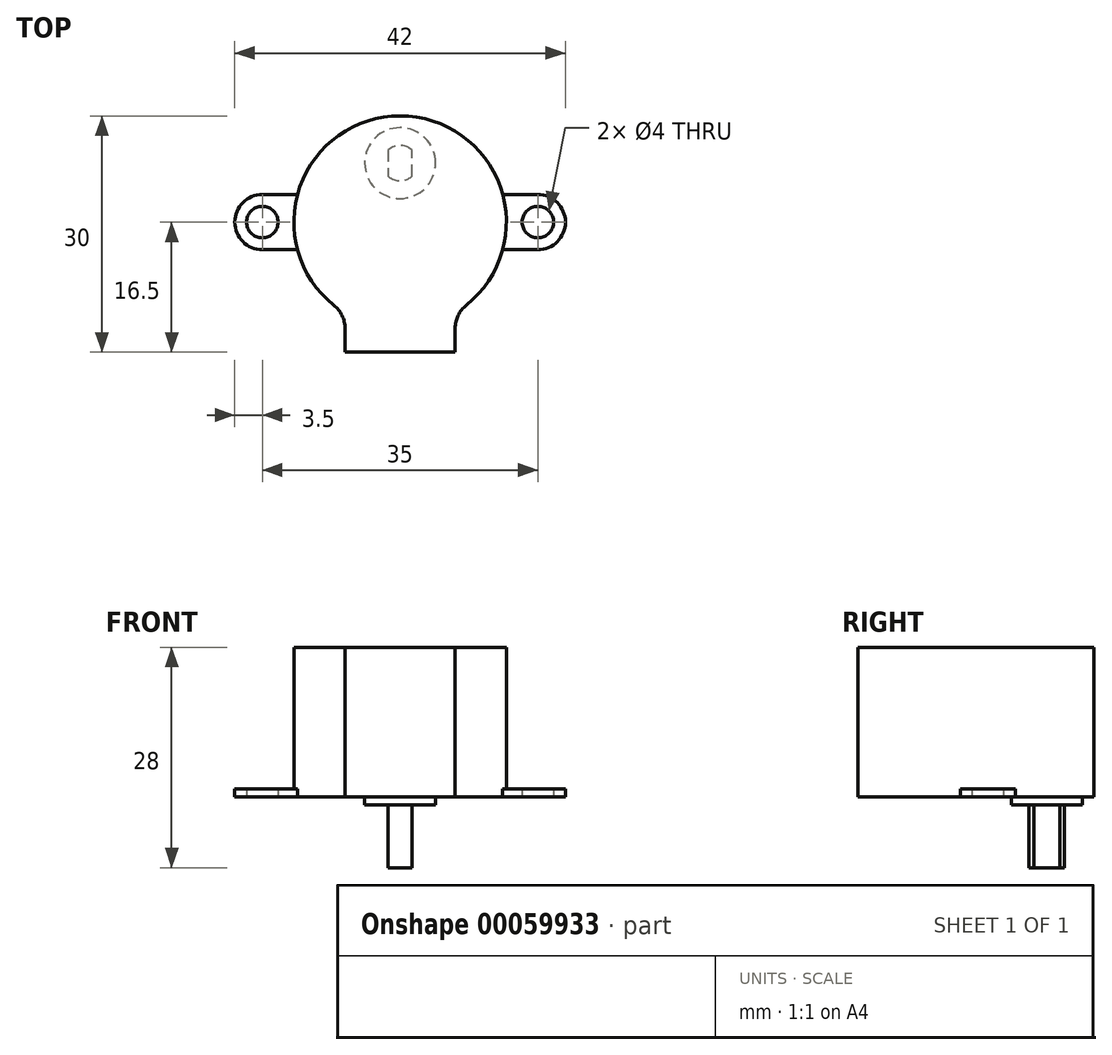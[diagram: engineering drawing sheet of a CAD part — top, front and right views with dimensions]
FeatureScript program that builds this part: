
annotation { "Feature Type Name" : "Feature", "Feature Type Description" : "" }
export const myFeature = defineFeature(function(context is Context, id is Id, definition is map)
    precondition{}
    {
        {
            var Q0;
            Q0=qCreatedBy(makeId("Top.planeOp"),FACE);
            var sketch = newSketch(context, id + "F0", { "sketchPlane" : qUnion([Q0])});
            skArc(sketch, "E0", {"start": v(8.42, -10.55) * mm, "mid": v(0, 13.5) * mm, "end": v(-8.42, -10.55) * mm});
            skLineSegment(sketch, "E1.bottom", {"start": v(-7, -13.5) * mm, "end": v(7, -13.5) * mm, "construction": true});
            skLineSegment(sketch, "E1.top", {"start": v(-7, -16.5) * mm, "end": v(7, -16.5) * mm});
            skLineSegment(sketch, "E1.left", {"start": v(-7, -13.5) * mm, "end": v(-7, -16.5) * mm});
            skLineSegment(sketch, "E1.right", {"start": v(7, -13.5) * mm, "end": v(7, -16.5) * mm});
            skLineSegment(sketch, "E2", {"start": v(0, -13.5) * mm, "end": v(0, -16.5) * mm, "construction": true});
            skArc(sketch, "E3", {"start": v(-7, -13.5) * mm, "mid": v(-7.37, -11.86) * mm, "end": v(-8.42, -10.55) * mm});
            skArc(sketch, "E4.MirrorCS", {"start": v(7, -13.5) * mm, "mid": v(7.37, -11.86) * mm, "end": v(8.42, -10.55) * mm});
            skSolve(sketch);
        }
        {
            var Q0;
            Q0=makeQuery(id+"F0.imprint","IMPRINT",FACE,{"disambiguationData":[TD([[makeQuery(id+"F0.imprint","IMPRINT",EDGE,{"derivedFrom":sQuery(id+"F0.wireOp",EDGE,"E0")}),1.0]])]});
            extrude(context, id + "F1", {"entities" : qUnion([Q0]), "depth" : 19 * mm});
        }
        {
            var Q0;
            Q0=qCreatedBy(makeId("Top.planeOp"),FACE);
            var sketch = newSketch(context, id + "F2", { "sketchPlane" : qUnion([Q0])});
            skCircle(sketch, "E5", {"center": v(17.5, 0) * mm, "radius": 2 * mm});
            skLineSegment(sketch, "E6", {"start": v(13.04, -3.5) * mm, "end": v(17.5, -3.5) * mm});
            skLineSegment(sketch, "E7", {"start": v(13.04, 3.5) * mm, "end": v(17.5, 3.5) * mm});
            skArc(sketch, "E8", {"start": v(17.5, -3.5) * mm, "mid": v(21, 0) * mm, "end": v(17.5, 3.5) * mm});
            skLineSegment(sketch, "E9", {"start": v(17.5, -3.5) * mm, "end": v(17.5, 0) * mm, "construction": true});
            skArc(sketch, "E10", {"start": v(13.04, -3.5) * mm, "mid": v(13.5, 0) * mm, "end": v(13.04, 3.5) * mm});
            skLineSegment(sketch, "E11.MirrorCS", {"start": v(-13.04, -3.5) * mm, "end": v(-17.5, -3.5) * mm});
            skArc(sketch, "E12.MirrorCS", {"start": v(-17.5, -3.5) * mm, "mid": v(-21, 0) * mm, "end": v(-17.5, 3.5) * mm});
            skCircle(sketch, "E13.MirrorC", {"center": v(-17.5, 0) * mm, "radius": 2 * mm});
            skLineSegment(sketch, "E14.MirrorCS", {"start": v(-13.04, 3.5) * mm, "end": v(-17.5, 3.5) * mm});
            skArc(sketch, "E15.MirrorCS", {"start": v(-13.04, -3.5) * mm, "mid": v(-13.5, 0) * mm, "end": v(-13.04, 3.5) * mm});
            skSolve(sketch);
        }
        {
            var Q0;
            Q0 = qSketchRegion(id + "F2", true);
            extrude(context, id + "F3", {"entities" : qUnion([Q0]), "operationType" : NewBodyOperationType.ADD, "depth" : 1 * mm});
        }
        {
            var Q0;
            Q0=makeQuery(id+"F3.boolean.opBoolean","MERGE",FACE,{"derivedFrom":[makeQuery(id+"F1.opExtrude","CAP_FACE",FACE,{"disambiguationData":[OSD([sQuery(id+"F0.wireOp",EDGE,"E0"),sQuery(id+"F0.wireOp",EDGE,"E1.top"),sQuery(id+"F0.wireOp",EDGE,"E1.left"),sQuery(id+"F0.wireOp",EDGE,"E1.right"),sQuery(id+"F0.wireOp",EDGE,"E3"),sQuery(id+"F0.wireOp",EDGE,"E4.MirrorCS")])],"isStart":true}),makeQuery(id+"F3.opExtrude","CAP_FACE",FACE,{"disambiguationData":[OSD([sQuery(id+"F2.wireOp",EDGE,"E5"),sQuery(id+"F2.wireOp",EDGE,"E6"),sQuery(id+"F2.wireOp",EDGE,"E7"),sQuery(id+"F2.wireOp",EDGE,"E8"),sQuery(id+"F2.wireOp",EDGE,"E10")])],"isStart":true}),makeQuery(id+"F3.opExtrude","CAP_FACE",FACE,{"disambiguationData":[OSD([sQuery(id+"F2.wireOp",EDGE,"E11.MirrorCS"),sQuery(id+"F2.wireOp",EDGE,"E12.MirrorCS"),sQuery(id+"F2.wireOp",EDGE,"E13.MirrorC"),sQuery(id+"F2.wireOp",EDGE,"E14.MirrorCS"),sQuery(id+"F2.wireOp",EDGE,"E15.MirrorCS")])],"isStart":true})]});
            var sketch = newSketch(context, id + "F4", { "sketchPlane" : qUnion([Q0])});
            skCircle(sketch, "E16", {"center": v(0, -7.5) * mm, "radius": 4.5 * mm});
            skSolve(sketch);
        }
        {
            var Q0;
            Q0=makeQuery(id+"F4.imprint","IMPRINT",FACE,{"disambiguationData":[TD([[makeQuery(id+"F4.imprint","IMPRINT",EDGE,{"derivedFrom":sQuery(id+"F4.wireOp",EDGE,"E16")}),1.0]])]});
            extrude(context, id + "F5", {"entities" : qUnion([Q0]), "operationType" : NewBodyOperationType.ADD, "depth" : 1 * mm});
        }
        {
            var Q0;
            Q0=makeQuery(id+"F5.opExtrude","CAP_FACE",FACE,{"disambiguationData":[OSD([sQuery(id+"F4.wireOp",EDGE,"E16")])],"isStart":false});
            var sketch = newSketch(context, id + "F6", { "sketchPlane" : qUnion([Q0])});
            skArc(sketch, "E17", {"start": v(-1.5, -9.18) * mm, "mid": v(0, -9.75) * mm, "end": v(1.5, -9.18) * mm});
            skLineSegment(sketch, "E18", {"start": v(-1.5, -9.18) * mm, "end": v(-1.5, -5.82) * mm});
            skLineSegment(sketch, "E19", {"start": v(1.5, -5.82) * mm, "end": v(1.5, -9.18) * mm});
            skArc(sketch, "E20.trimOffspring", {"start": v(1.5, -5.82) * mm, "mid": v(0, -5.25) * mm, "end": v(-1.5, -5.82) * mm});
            skSolve(sketch);
        }
        {
            var Q0;
            Q0=makeQuery(id+"F6.imprint","IMPRINT",FACE,{"disambiguationData":[TD([[makeQuery(id+"F6.imprint","IMPRINT",EDGE,{"derivedFrom":sQuery(id+"F6.wireOp",EDGE,"E17")}),1.0]])]});
            extrude(context, id + "F7", {"entities" : qUnion([Q0]), "operationType" : NewBodyOperationType.ADD, "depth" : 8 * mm});
        }
    });
